# Revit family: EKF_EE_ПерегородкиДляСборкиГоризонтальныхШинTrivia_AVERES
name_source: partatom
category: Электрооборудование
units: mm (PartAtom-declared; Revit-internal decimal feet)

## family parameters
Всегда вертикально = Нет
На основе рабочей плоскости = Да
Общий = Да
При загрузке вырезать с полостями = Нет
Размер круглого соединителя = Использовать диаметр
Тип детали = Силовой щит
Точка расчета площади = Нет

## types (15) — shared parameters
ADSK_Единица измерения = шт.
ADSK_Завод-изготовитель = EKF
ADSK_Количество = 1
ADSK_Материал = RAL 7035_Сталь
ADSK_Размер_Высота = 225 мм
Глубина = 400 мм
Изготовитель = EKF
Отметка по умолчанию = 1219.2 мм
Серия номенклатуры = Averes
Степень защиты IP = -
ТВ = EKF_2_TRIVIA_AVERES
Тип установки = -
Шаг_НабораПластронов_2шт = 100 мм
zero-valued in all types: ADSK_Масса

## per-type parameters (varying)
| type | ADSK_Код изделия | ADSK_Размер_Глубина | ADSK_Размер_Ширина | Тип |
| Перегородки для сборки горизонтальных шин Ш200 EKF AVERES | PCHB2 | 600 мм | 200 мм | 735 мм |
| Перегородки для сборки горизонтальных шин Ш200 Г400 EKF AVERES | PCHB24 | 400 мм | 200 мм | 736 мм |
| Перегородки для сборки горизонтальных шин Ш200 Г800 EKF AVERES | PCHB28 | 800 мм | 200 мм | 737 мм |
| Перегородки для сборки горизонтальных шин Ш300 Г400 EKF AVERES | PCHB34 | 400 мм | 300 мм | 738 мм |
| Перегородки для сборки горизонтальных шин Ш300 Г600 EKF AVERES | PCHB3 | 600 мм | 300 мм | 739 мм |
| Перегородки для сборки горизонтальных шин Ш300 Г800 EKF AVERES | PCHB38 | 800 мм | 300 мм | 740 мм |
| Перегородки для сборки горизонтальных шин Ш400 EKF AVERES | PCHB4 | 600 мм | 400 мм | 741 мм |
| Перегородки для сборки горизонтальных шин Ш400 Г400 EKF AVERES | PCHB44 | 400 мм | 400 мм | 742 мм |
| Перегородки для сборки горизонтальных шин Ш400 Г800 EKF AVERES | PCHB48 | 800 мм | 400 мм | 743 мм |
| Перегородки для сборки горизонтальных шин Ш600 EKF AVERES | PCHB6 | 600 мм | 600 мм | 744 мм |
| Перегородки для сборки горизонтальных шин Ш600 Г400 EKF AVERES | PCHB64 | 400 мм | 600 мм | 745 мм |
| Перегородки для сборки горизонтальных шин Ш600 Г800 EKF AVERES | PCHB68 | 800 мм | 600 мм | 746 мм |
| Перегородки для сборки горизонтальных шин Ш800 EKF AVERES | PCHB8 | 600 мм | 800 мм | 747 мм |
| Перегородки для сборки горизонтальных шин Ш800 Г400 EKF AVERES | PCHB84 | 400 мм | 800 мм | 748 мм |
| Перегородки для сборки горизонтальных шин Ш800 Г800 EKF AVERES | PCHB88 | 800 мм | 800 мм | 749 мм |

note: column(s) folded — value = type name in every type: ADSK_Марка, ADSK_Наименование, ADSK_Обозначение
